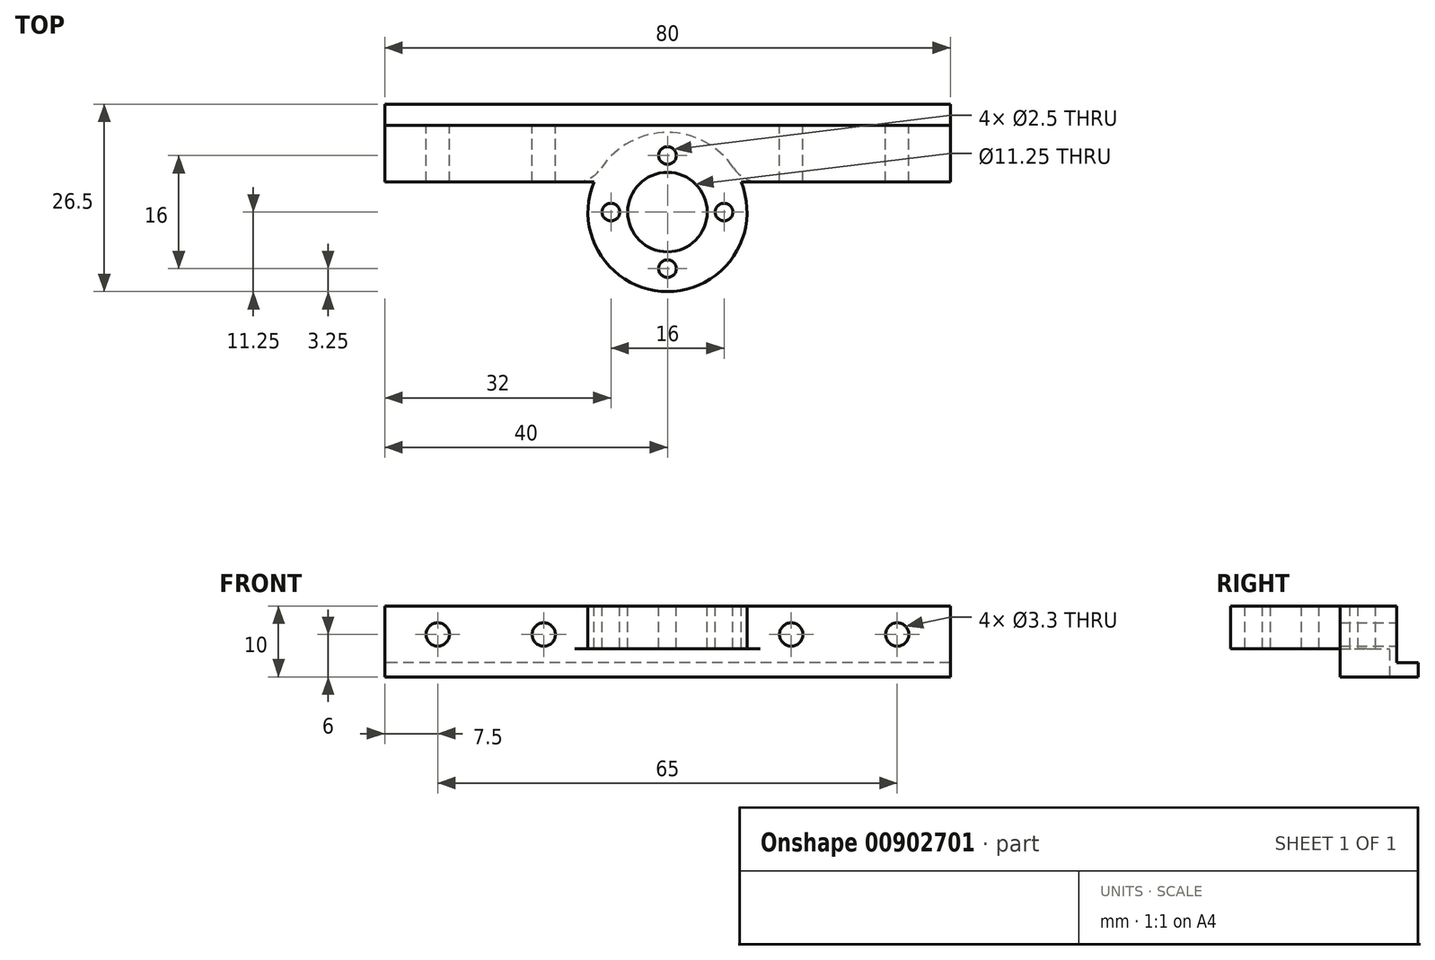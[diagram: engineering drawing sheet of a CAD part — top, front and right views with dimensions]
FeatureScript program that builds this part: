
annotation { "Feature Type Name" : "Feature", "Feature Type Description" : "" }
export const myFeature = defineFeature(function(context is Context, id is Id, definition is map)
    precondition{}
    {
        {
            var Q0;
            Q0=qCreatedBy(makeId("Front.planeOp"),FACE);
            var sketch = newSketch(context, id + "F0", { "sketchPlane" : qUnion([Q0])});
            skLineSegment(sketch, "E0", {"start": v(3.5, 1.85) * mm, "end": v(5.12, 1.85) * mm});
            skLineSegment(sketch, "E1", {"start": v(5.12, 1.85) * mm, "end": v(5.12, 0) * mm});
            skLineSegment(sketch, "E2", {"start": v(5.13, 0) * mm, "end": v(11.25, 0) * mm});
            skLineSegment(sketch, "E3", {"start": v(11.25, 0) * mm, "end": v(11.25, -6) * mm});
            skLineSegment(sketch, "E4", {"start": v(11.25, -6) * mm, "end": v(5.12, -6) * mm});
            skLineSegment(sketch, "E5", {"start": v(5.12, -6) * mm, "end": v(5.12, -16.15) * mm});
            skLineSegment(sketch, "E6", {"start": v(5.12, -16.15) * mm, "end": v(3.5, -16.15) * mm});
            skLineSegment(sketch, "E7", {"start": v(3.5, -16.15) * mm, "end": v(3.5, 1.85) * mm});
            skLineSegment(sketch, "E8", {"start": v(0, 0) * mm, "end": v(0, -24.26) * mm, "construction": true});
            skSolve(sketch);
        }
        {
            var Q0;
            Q0=qSketchRegion(id+"F0",true);
            var Q1;
            Q1=sQuery(id+"F0.wireOp",EDGE,"E8");
            revolve(context, id + "F1", {"surfaceOperationType" : NewSurfaceOperationType.NEW, "entities" : qUnion([Q0]), "axis" : qUnion([Q1]), "revolveType" : RevolveType.FULL});
        }
        {
            var Q0;
            Q0=makeQuery(id+"F1.opRevolve","SWEPT_FACE",FACE,{"disambiguationData":[OSD([sQuery(id+"F0.wireOp",EDGE,"E2")])]});
            var sketch = newSketch(context, id + "F2", { "sketchPlane" : qUnion([Q0])});
            skCircle(sketch, "E9", {"center": v(0, 8) * mm, "radius": 1.75 * mm, "construction": true});
            skLineSegment(sketch, "E10", {"start": v(0, 0) * mm, "end": v(0, 8) * mm, "construction": true});
            skCircle(sketch, "E11.1.0", {"center": v(-8, 0) * mm, "radius": 1.75 * mm, "construction": true});
            skCircle(sketch, "E11.2.0", {"center": v(0, -8) * mm, "radius": 1.75 * mm, "construction": true});
            skCircle(sketch, "E11.3.0", {"center": v(8, 0) * mm, "radius": 1.75 * mm, "construction": true});
            skPoint(sketch, "E11.center", {"position": v(0, 0) * mm});
            skSolve(sketch);
        }
        {
            var Q0;
            Q0=makeQuery(id+"F1.opRevolve","SWEPT_FACE",FACE,{"disambiguationData":[OSD([sQuery(id+"F0.wireOp",EDGE,"E0")])]});
            var sketch = newSketch(context, id + "F3", { "sketchPlane" : qUnion([Q0])});
            skCircle(sketch, "E12", {"center": v(0, 0) * mm, "radius": 5.62 * mm});
            skSolve(sketch);
        }
        {
            var Q0;
            Q0=sQuery(id+"F2.wireOp",VERTEX,"E9.center");
            var Q1;
            Q1=sQuery(id+"F2.wireOp",VERTEX,"E11.3.0.center");
            var Q2;
            Q2=sQuery(id+"F2.wireOp",VERTEX,"E11.2.0.center");
            var Q3;
            Q3=sQuery(id+"F2.wireOp",VERTEX,"E11.1.0.center");
            var Q4;
            Q4=makeQuery(id+"F1.opRevolve","SWEPT_BODY",BODY,{"disambiguationData":[OSD([sQuery(id+"F0.wireOp",EDGE,"E0"),sQuery(id+"F0.wireOp",EDGE,"E1"),sQuery(id+"F0.wireOp",EDGE,"E2"),sQuery(id+"F0.wireOp",EDGE,"E3"),sQuery(id+"F0.wireOp",EDGE,"E4"),sQuery(id+"F0.wireOp",EDGE,"E5"),sQuery(id+"F0.wireOp",EDGE,"E6"),sQuery(id+"F0.wireOp",EDGE,"E7")])]});
            hole(context, id + "F4", {"style" : HoleStyle.SIMPLE, "endStyle" : HoleEndStyle.THROUGH, "standardTappedOrClearance" : lookupTablePath({ "standard" : "ISO", "fit" : "Normal", "engagement" : "75%", "pitch" : "0.5 mm", "size" : "M3", "type" : "Tapped" }), "standardBlindInLast" : lookupTablePath({ "fit" : "Normal", "standard" : "ISO", "engagement" : "75%", "pitch" : "0.5 mm", "size" : "M3", "type" : "Tapped" }), "holeDiameter" : 2.5 * mm, "majorDiameter" : 3 * mm, "showTappedDepth" : true, "isTappedThrough" : true, "tappedDepth" : 12 * mm, "tapClearance" : 3, "locations" : qUnion([Q0, Q1, Q2, Q3]), "scope" : qUnion([Q4])});
        }
        {
            var Q0;
            Q0 = qSketchRegion(id + "F3", true);
            extrude(context, id + "F5", {"entities" : qUnion([Q0]), "operationType" : NewBodyOperationType.REMOVE, "endBound" : BoundingType.THROUGH_ALL, "oppositeDirection" : true, "depth" : 25 * mm, "offsetDistance" : 25 * mm});
        }
        {
            var Q0;
            Q0=makeQuery(id+"F1.opRevolve","SWEPT_FACE",FACE,{"disambiguationData":[OSD([sQuery(id+"F0.wireOp",EDGE,"E2")])]});
            var sketch = newSketch(context, id + "F6", { "sketchPlane" : qUnion([Q0])});
            skLineSegment(sketch, "E13", {"start": v(10.42, 4.25) * mm, "end": v(40, 4.25) * mm});
            skLineSegment(sketch, "E14", {"start": v(40, 4.25) * mm, "end": v(40, 12.25) * mm});
            skLineSegment(sketch, "E15", {"start": v(40, 12.25) * mm, "end": v(-40, 12.25) * mm});
            skLineSegment(sketch, "E16", {"start": v(-40, 12.25) * mm, "end": v(-40, 4.25) * mm});
            skLineSegment(sketch, "E17", {"start": v(-40, 4.25) * mm, "end": v(-10.42, 4.25) * mm});
            skSolve(sketch);
        }
        {
            var Q0;
            {var subQ0=sQuery(id+"F6.wireOp",EDGE,"E13");Q0=makeQuery(id+"F6.imprint","IMPRINT",FACE,{"disambiguationData":[TD([[makeQuery(id+"F6.imprint","IMPRINT",EDGE,{"derivedFrom":subQ0}),1.0]])]});}
            var Q1;
            Q1=makeQuery(id+"F1.opRevolve","SWEPT_FACE",FACE,{"disambiguationData":[OSD([sQuery(id+"F0.wireOp",EDGE,"E4")])]});
            extrude(context, id + "F7", {"entities" : qUnion([Q0]), "operationType" : NewBodyOperationType.ADD, "oppositeDirection" : true, "depth" : 10 * mm, "endBoundEntityFace" : qUnion([Q1]), "offsetDistance" : 25 * mm});
        }
        {
            var Q0;
            {var subQ0=sQuery(id+"F0.wireOp",EDGE,"E3");var subQ1=sQuery(id+"F6.wireOp",EDGE,"E13");Q0=makeQuery(id+"F7.boolean.opBoolean","SPLIT",EDGE,{"disambiguationData":[topologyDisambiguationEdgeConnected([makeQuery(id+"F1.opRevolve","SWEPT_FACE",FACE,{"disambiguationData":[OSD([subQ0])]})])],"derivedFrom":makeQuery(id+"F7.opExtrude","SWEPT_EDGE",EDGE,{"disambiguationData":[OSD([sQuery(id+"F0.wireOp",EDGE,"E2"),subQ0,subQ1])]})});}
            var Q1;
            {var subQ0=sQuery(id+"F0.wireOp",EDGE,"E3");var subQ1=sQuery(id+"F6.wireOp",EDGE,"E17");Q1=makeQuery(id+"F7.boolean.opBoolean","SPLIT",EDGE,{"disambiguationData":[topologyDisambiguationEdgeConnected([makeQuery(id+"F1.opRevolve","SWEPT_FACE",FACE,{"disambiguationData":[OSD([subQ0])]})])],"derivedFrom":makeQuery(id+"F7.opExtrude","SWEPT_EDGE",EDGE,{"disambiguationData":[OSD([sQuery(id+"F0.wireOp",EDGE,"E2"),subQ0,subQ1])]})});}
            fillet(context, id + "F8", {"entities" : qUnion([Q0, Q1]), "radius" : 4.5 * mm, "tangentPropagation" : true, "allowEdgeOverflow" : false});
        }
        {
            var Q0;
            Q0=makeQuery(id+"F7.opExtrude","SWEPT_FACE",FACE,{"disambiguationData":[OSD([sQuery(id+"F6.wireOp",EDGE,"E15")])]});
            var sketch = newSketch(context, id + "F9", { "sketchPlane" : qUnion([Q0])});
            skLineSegment(sketch, "E18.bottom", {"start": v(-40, -10) * mm, "end": v(40, -10) * mm});
            skLineSegment(sketch, "E18.top", {"start": v(-40, -8) * mm, "end": v(40, -8) * mm});
            skLineSegment(sketch, "E18.left", {"start": v(-40, -10) * mm, "end": v(-40, -8) * mm});
            skLineSegment(sketch, "E18.right", {"start": v(40, -10) * mm, "end": v(40, -8) * mm});
            skSolve(sketch);
        }
        {
            var Q0;
            Q0 = qSketchRegion(id + "F9", true);
            extrude(context, id + "F10", {"entities" : qUnion([Q0]), "operationType" : NewBodyOperationType.ADD, "depth" : 3 * mm, "offsetDistance" : 25 * mm});
        }
        {
            var Q0;
            Q0=makeQuery(id+"F7.opExtrude","SWEPT_FACE",FACE,{"disambiguationData":[OSD([sQuery(id+"F6.wireOp",EDGE,"E15")])]});
            var sketch = newSketch(context, id + "F11", { "sketchPlane" : qUnion([Q0])});
            skLineSegment(sketch, "E19", {"start": v(-40, -4) * mm, "end": v(-32.5, -4) * mm, "construction": true});
            skLineSegment(sketch, "E20", {"start": v(-32.5, -4) * mm, "end": v(-17.5, -4) * mm, "construction": true});
            skLineSegment(sketch, "E21", {"start": v(-17.5, -4) * mm, "end": v(17.5, -4) * mm, "construction": true});
            skLineSegment(sketch, "E22", {"start": v(17.5, -4) * mm, "end": v(32.5, -4) * mm, "construction": true});
            skLineSegment(sketch, "E23", {"start": v(32.5, -4) * mm, "end": v(40, -4) * mm, "construction": true});
            skPoint(sketch, "E24", {"position": v(-32.5, -4) * mm});
            skPoint(sketch, "E25", {"position": v(-17.5, -4) * mm});
            skPoint(sketch, "E26", {"position": v(17.5, -4) * mm});
            skPoint(sketch, "E27", {"position": v(32.5, -4) * mm});
            skSolve(sketch);
        }
        {
            var Q0;
            Q0=sQuery(id+"F11.wireOp",VERTEX,"E24");
            var Q1;
            Q1=sQuery(id+"F11.wireOp",VERTEX,"E25");
            var Q2;
            Q2=sQuery(id+"F11.wireOp",VERTEX,"E26");
            var Q3;
            Q3=sQuery(id+"F11.wireOp",VERTEX,"E27");
            var Q4;
            Q4=makeQuery(id+"F1.opRevolve","SWEPT_BODY",BODY,{"disambiguationData":[OSD([sQuery(id+"F0.wireOp",EDGE,"E0"),sQuery(id+"F0.wireOp",EDGE,"E1"),sQuery(id+"F0.wireOp",EDGE,"E2"),sQuery(id+"F0.wireOp",EDGE,"E3"),sQuery(id+"F0.wireOp",EDGE,"E4"),sQuery(id+"F0.wireOp",EDGE,"E5"),sQuery(id+"F0.wireOp",EDGE,"E6"),sQuery(id+"F0.wireOp",EDGE,"E7")])]});
            hole(context, id + "F12", {"style" : HoleStyle.SIMPLE, "endStyle" : HoleEndStyle.THROUGH, "standardTappedOrClearance" : lookupTablePath({ "standard" : "ISO", "fit" : "Normal", "engagement" : "75%", "pitch" : "0.7 mm", "size" : "M4", "type" : "Tapped" }), "standardBlindInLast" : lookupTablePath({ "fit" : "Normal", "standard" : "ISO", "engagement" : "75%", "pitch" : "0.7 mm", "size" : "M4", "type" : "Tapped" }), "holeDiameter" : 3.3 * mm, "majorDiameter" : 4 * mm, "showTappedDepth" : true, "isTappedThrough" : true, "tappedDepth" : 12 * mm, "tapClearance" : 3, "locations" : qUnion([Q0, Q1, Q2, Q3]), "scope" : qUnion([Q4])});
        }
    });
